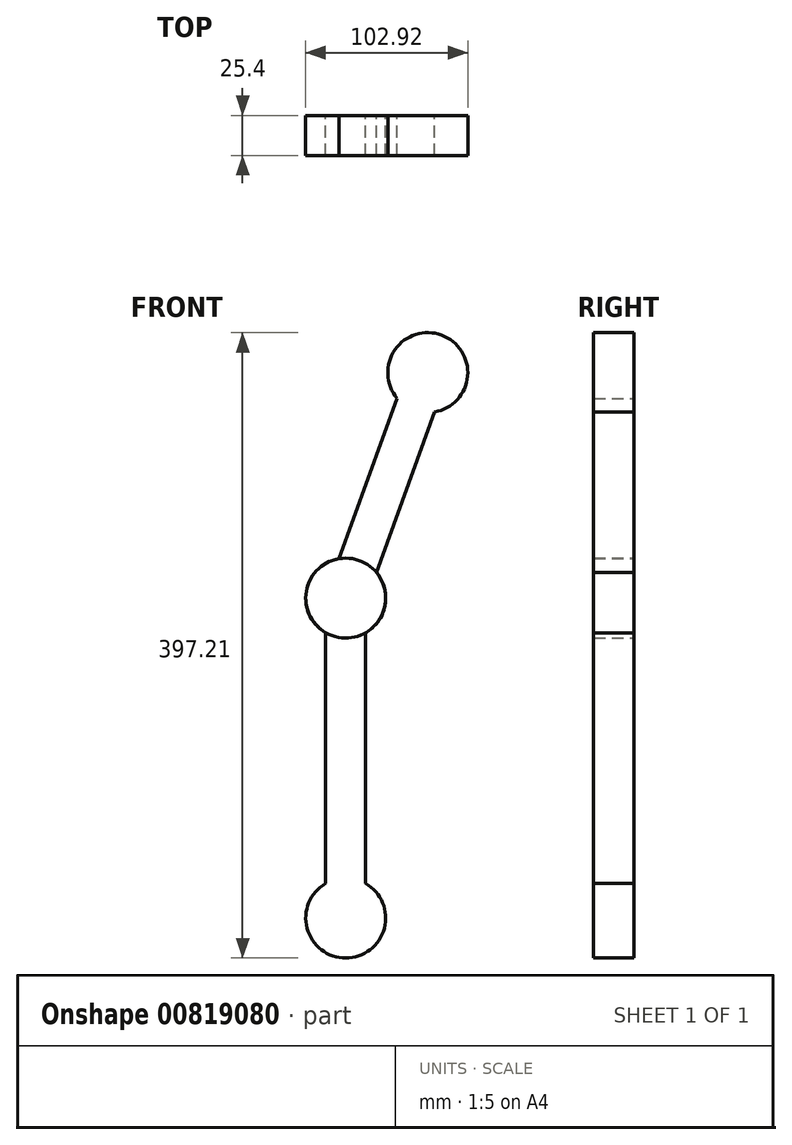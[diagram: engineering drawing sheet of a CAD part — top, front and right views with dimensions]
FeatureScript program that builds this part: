
annotation { "Feature Type Name" : "Feature", "Feature Type Description" : "" }
export const myFeature = defineFeature(function(context is Context, id is Id, definition is map)
    precondition{}
    {
        {
            var Q0;
            Q0=qCreatedBy(makeId("Front.planeOp"),FACE);
            var sketch = newSketch(context, id + "F0", { "sketchPlane" : qUnion([Q0])});
            skCircle(sketch, "E0", {"center": v(0, 0) * mm, "radius": 25.4 * mm});
            skCircle(sketch, "E1", {"center": v(0, -203.2) * mm, "radius": 25.4 * mm});
            skLineSegment(sketch, "E2", {"start": v(0, 0) * mm, "end": v(0, -203.2) * mm});
            skPoint(sketch, "E3.start.orphan", {"position": v(0, 152.4) * mm});
            skCircle(sketch, "E4", {"center": v(52.12, 143.2) * mm, "radius": 25.4 * mm});
            skLineSegment(sketch, "E5", {"start": v(52.12, 143.2) * mm, "end": v(0, 0) * mm});
            skLineSegment(sketch, "E6.0", {"start": v(40.19, 147.55) * mm, "end": v(-11.93, 4.34) * mm});
            skLineSegment(sketch, "E7.0", {"start": v(64.06, 138.87) * mm, "end": v(11.93, -4.34) * mm});
            skLineSegment(sketch, "E8.0", {"start": v(-12.7, 0) * mm, "end": v(-12.7, -203.2) * mm});
            skLineSegment(sketch, "E9.0", {"start": v(12.7, 0) * mm, "end": v(12.7, -203.2) * mm});
            skSolve(sketch);
        }
        {
            var Q0;
            {var subQ0=sQuery(id+"F0.wireOp",EDGE,"E9.0");var subQ1=sQuery(id+"F0.wireOp",EDGE,"E0");var subQ2=makeQuery(id+"F0.imprint","INTERSECT",VERTEX,{"derivedFrom":[subQ1,subQ0]});Q0=makeQuery(id+"F0.imprint","IMPRINT",FACE,{"disambiguationData":[TD([[makeQuery(id+"F0.imprint","IMPRINT",EDGE,{"disambiguationData":[TD([[subQ2,1.0]])],"derivedFrom":subQ1}),-1.0]])]});}
            var Q1;
            {var subQ0=sQuery(id+"F0.wireOp",EDGE,"E1");var subQ1=makeQuery(id+"F0.imprint","INTERSECT",VERTEX,{"derivedFrom":[subQ0,sQuery(id+"F0.wireOp",EDGE,"E9.0")]});Q1=makeQuery(id+"F0.imprint","IMPRINT",FACE,{"disambiguationData":[TD([[makeQuery(id+"F0.imprint","IMPRINT",EDGE,{"disambiguationData":[TD([[subQ1,-1.0]])],"derivedFrom":subQ0}),1.0]])]});}
            var Q2;
            {var subQ0=sQuery(id+"F0.wireOp",EDGE,"E8.0");var subQ1=sQuery(id+"F0.wireOp",EDGE,"E0");var subQ2=makeQuery(id+"F0.imprint","INTERSECT",VERTEX,{"derivedFrom":[subQ1,subQ0]});Q2=makeQuery(id+"F0.imprint","IMPRINT",FACE,{"disambiguationData":[TD([[makeQuery(id+"F0.imprint","IMPRINT",EDGE,{"disambiguationData":[TD([[subQ2,-1.0]])],"derivedFrom":subQ1}),-1.0]])]});}
            var Q3;
            {var subQ3=sQuery(id+"F0.wireOp",EDGE,"E0");var subQ6=sQuery(id+"F0.wireOp",EDGE,"E7.0");var subQ10=makeQuery(id+"F0.imprint","INTERSECT",VERTEX,{"derivedFrom":[subQ3,subQ6]});Q3=makeQuery(id+"F0.imprint","IMPRINT",FACE,{"disambiguationData":[TD([[makeQuery(id+"F0.imprint","IMPRINT",EDGE,{"disambiguationData":[TD([[subQ10,-1.0]])],"derivedFrom":subQ3}),1.0]])]});}
            var Q4;
            {var subQ3=sQuery(id+"F0.wireOp",EDGE,"E0");var subQ6=makeQuery(id+"F0.imprint","INTERSECT",VERTEX,{"derivedFrom":[subQ3,sQuery(id+"F0.wireOp",EDGE,"E6.0")]});Q4=makeQuery(id+"F0.imprint","IMPRINT",FACE,{"disambiguationData":[TD([[makeQuery(id+"F0.imprint","IMPRINT",EDGE,{"disambiguationData":[TD([[subQ6,1.0]])],"derivedFrom":subQ3}),1.0]])]});}
            var Q5;
            {var subQ0=sQuery(id+"F0.wireOp",EDGE,"E7.0");var subQ1=sQuery(id+"F0.wireOp",EDGE,"E0");var subQ2=makeQuery(id+"F0.imprint","INTERSECT",VERTEX,{"derivedFrom":[subQ1,subQ0]});Q5=makeQuery(id+"F0.imprint","IMPRINT",FACE,{"disambiguationData":[TD([[makeQuery(id+"F0.imprint","IMPRINT",EDGE,{"disambiguationData":[TD([[subQ2,1.0]])],"derivedFrom":subQ1}),1.0]])]});}
            extrude(context, id + "F1", {"entities" : qUnion([Q0, Q1, Q2, Q3, Q4, Q5]), "depth" : 25.4 * mm, "offsetDistance" : 25.4 * mm});
        }
        {
            var Q0;
            {var subQ0=sQuery(id+"F0.wireOp",EDGE,"E4");var subQ1=makeQuery(id+"F0.imprint","INTERSECT",VERTEX,{"derivedFrom":[subQ0,sQuery(id+"F0.wireOp",EDGE,"E6.0")]});Q0=makeQuery(id+"F0.imprint","IMPRINT",FACE,{"disambiguationData":[TD([[makeQuery(id+"F0.imprint","IMPRINT",EDGE,{"disambiguationData":[TD([[subQ1,-1.0]])],"derivedFrom":subQ0}),1.0]])]});}
            var Q1;
            {var subQ0=sQuery(id+"F0.wireOp",EDGE,"E7.0");var subQ1=sQuery(id+"F0.wireOp",EDGE,"E0");var subQ2=makeQuery(id+"F0.imprint","INTERSECT",VERTEX,{"derivedFrom":[subQ1,subQ0]});Q1=makeQuery(id+"F0.imprint","IMPRINT",FACE,{"disambiguationData":[TD([[makeQuery(id+"F0.imprint","IMPRINT",EDGE,{"disambiguationData":[TD([[subQ2,-1.0]])],"derivedFrom":subQ1}),-1.0]])]});}
            var Q2;
            {var subQ0=sQuery(id+"F0.wireOp",EDGE,"E6.0");var subQ1=sQuery(id+"F0.wireOp",EDGE,"E0");var subQ2=makeQuery(id+"F0.imprint","INTERSECT",VERTEX,{"derivedFrom":[subQ1,subQ0]});Q2=makeQuery(id+"F0.imprint","IMPRINT",FACE,{"disambiguationData":[TD([[makeQuery(id+"F0.imprint","IMPRINT",EDGE,{"disambiguationData":[TD([[subQ2,1.0]])],"derivedFrom":subQ1}),-1.0]])]});}
            var Q3;
            {var subQ0=sQuery(id+"F0.wireOp",EDGE,"E7.0");var subQ1=sQuery(id+"F0.wireOp",EDGE,"E0");var subQ2=makeQuery(id+"F0.imprint","INTERSECT",VERTEX,{"derivedFrom":[subQ1,subQ0]});Q3=makeQuery(id+"F0.imprint","IMPRINT",FACE,{"disambiguationData":[TD([[makeQuery(id+"F0.imprint","IMPRINT",EDGE,{"disambiguationData":[TD([[subQ2,1.0]])],"derivedFrom":subQ1}),1.0]])]});}
            var Q4;
            {var subQ3=sQuery(id+"F0.wireOp",EDGE,"E0");var subQ6=sQuery(id+"F0.wireOp",EDGE,"E7.0");var subQ10=makeQuery(id+"F0.imprint","INTERSECT",VERTEX,{"derivedFrom":[subQ3,subQ6]});Q4=makeQuery(id+"F0.imprint","IMPRINT",FACE,{"disambiguationData":[TD([[makeQuery(id+"F0.imprint","IMPRINT",EDGE,{"disambiguationData":[TD([[subQ10,-1.0]])],"derivedFrom":subQ3}),1.0]])]});}
            var Q5;
            {var subQ3=sQuery(id+"F0.wireOp",EDGE,"E0");var subQ6=makeQuery(id+"F0.imprint","INTERSECT",VERTEX,{"derivedFrom":[subQ3,sQuery(id+"F0.wireOp",EDGE,"E6.0")]});Q5=makeQuery(id+"F0.imprint","IMPRINT",FACE,{"disambiguationData":[TD([[makeQuery(id+"F0.imprint","IMPRINT",EDGE,{"disambiguationData":[TD([[subQ6,1.0]])],"derivedFrom":subQ3}),1.0]])]});}
            extrude(context, id + "F2", {"entities" : qUnion([Q0, Q1, Q2, Q3, Q4, Q5]), "depth" : 25.4 * mm, "offsetDistance" : 25.4 * mm});
        }
    });
